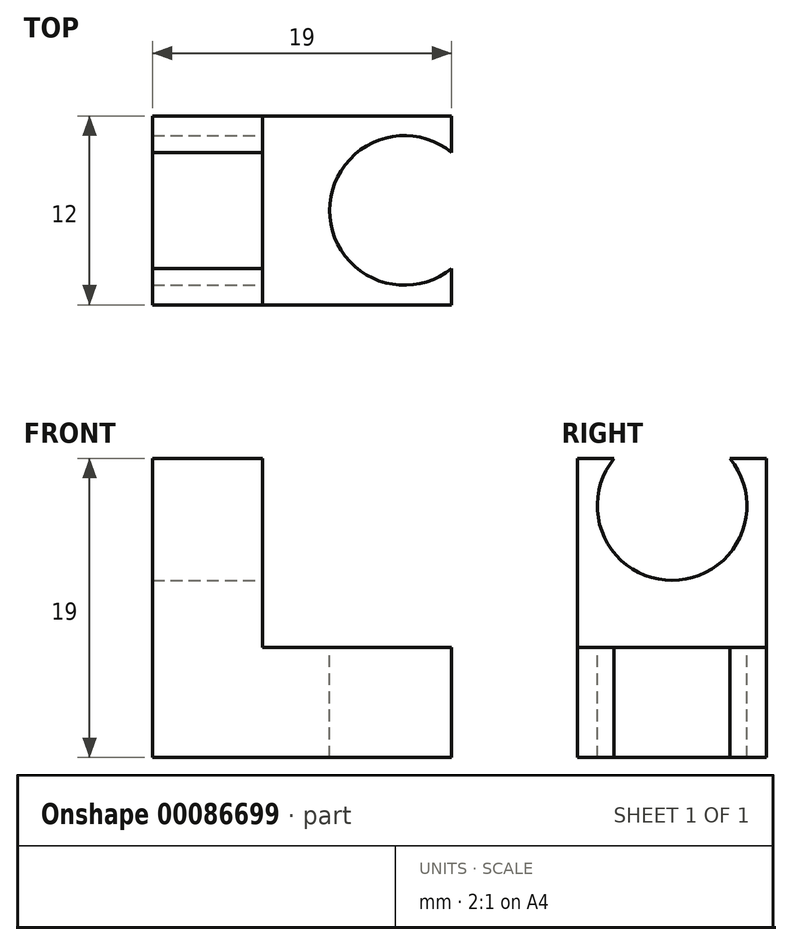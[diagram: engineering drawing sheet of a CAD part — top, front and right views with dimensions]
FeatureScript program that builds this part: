
annotation { "Feature Type Name" : "Feature", "Feature Type Description" : "" }
export const myFeature = defineFeature(function(context is Context, id is Id, definition is map)
    precondition{}
    {
        {
            var Q0;
            Q0=qCreatedBy(makeId("Front.planeOp"),FACE);
            var sketch = newSketch(context, id + "F0", { "sketchPlane" : qUnion([Q0])});
            skLineSegment(sketch, "E0", {"start": v(0, 19) * mm, "end": v(0, 0) * mm});
            skLineSegment(sketch, "E1", {"start": v(0, 0) * mm, "end": v(19, 0) * mm});
            skLineSegment(sketch, "E2", {"start": v(19, 0) * mm, "end": v(19, 7) * mm});
            skLineSegment(sketch, "E3", {"start": v(19, 7) * mm, "end": v(7, 7) * mm});
            skLineSegment(sketch, "E4", {"start": v(7, 7) * mm, "end": v(7, 19) * mm});
            skLineSegment(sketch, "E5", {"start": v(7, 19) * mm, "end": v(0, 19) * mm});
            skSolve(sketch);
        }
        {
            var Q0;
            Q0=makeQuery(id+"F0.imprint","IMPRINT",FACE,{"disambiguationData":[TD([[makeQuery(id+"F0.imprint","IMPRINT",EDGE,{"derivedFrom":sQuery(id+"F0.wireOp",EDGE,"E0")}),1.0]])]});
            extrude(context, id + "F1", {"entities" : qUnion([Q0]), "endBound" : BoundingType.SYMMETRIC, "depth" : 12 * mm});
        }
        {
            var Q0;
            Q0=makeQuery(id+"F1.opExtrude","SWEPT_FACE",FACE,{"disambiguationData":[OSD([sQuery(id+"F0.wireOp",EDGE,"E3")])]});
            var sketch = newSketch(context, id + "F2", { "sketchPlane" : qUnion([Q0])});
            skCircle(sketch, "E6", {"center": v(16, 0) * mm, "radius": 4.75 * mm});
            skSolve(sketch);
        }
        {
            var Q0;
            {var subQ0=sQuery(id+"F2.wireOp",EDGE,"E6");var subQ1=makeQuery(id+"F1.opExtrude","SWEPT_EDGE",EDGE,{"disambiguationData":[OSD([sQuery(id+"F0.wireOp",EDGE,"E2"),sQuery(id+"F0.wireOp",EDGE,"E3")])]});var subQ2=makeQuery(id+"F2.imprint","INTERSECT",VERTEX,{"disambiguationData":[OD(0.0)],"derivedFrom":[subQ1,subQ0]});Q0=makeQuery(id+"F2.imprint","IMPRINT",FACE,{"disambiguationData":[TD([[makeQuery(id+"F2.imprint","IMPRINT",EDGE,{"disambiguationData":[TD([[subQ2,1.0]])],"derivedFrom":subQ0}),1.0]])]});}
            var Q1;
            {var subQ0=sQuery(id+"F2.wireOp",EDGE,"E6");var subQ1=makeQuery(id+"F1.opExtrude","SWEPT_EDGE",EDGE,{"disambiguationData":[OSD([sQuery(id+"F0.wireOp",EDGE,"E2"),sQuery(id+"F0.wireOp",EDGE,"E3")])]});var subQ2=makeQuery(id+"F2.imprint","INTERSECT",VERTEX,{"disambiguationData":[OD(0.0)],"derivedFrom":[subQ1,subQ0]});Q1=makeQuery(id+"F2.imprint","IMPRINT",FACE,{"disambiguationData":[TD([[makeQuery(id+"F2.imprint","IMPRINT",EDGE,{"disambiguationData":[TD([[subQ2,-1.0]])],"derivedFrom":subQ0}),1.0]])]});}
            var Q2;
            Q2=sQuery(id+"F2.wireOp",EDGE,"E6");
            extrude(context, id + "F3", {"entities" : qUnion([Q0, Q1]), "operationType" : NewBodyOperationType.REMOVE, "surfaceEntities" : qUnion([Q2]), "endBound" : BoundingType.THROUGH_ALL, "oppositeDirection" : true, "depth" : 25 * mm});
        }
        {
            var Q0;
            Q0=makeQuery(id+"F1.opExtrude","SWEPT_FACE",FACE,{"disambiguationData":[OSD([sQuery(id+"F0.wireOp",EDGE,"E4")])]});
            var sketch = newSketch(context, id + "F4", { "sketchPlane" : qUnion([Q0])});
            skCircle(sketch, "E7", {"center": v(0, 16) * mm, "radius": 4.75 * mm});
            skSolve(sketch);
        }
        {
            var Q0;
            Q0 = qSketchRegion(id + "F4", true);
            extrude(context, id + "F5", {"entities" : qUnion([Q0]), "operationType" : NewBodyOperationType.REMOVE, "oppositeDirection" : true, "depth" : 25 * mm});
        }
    });
